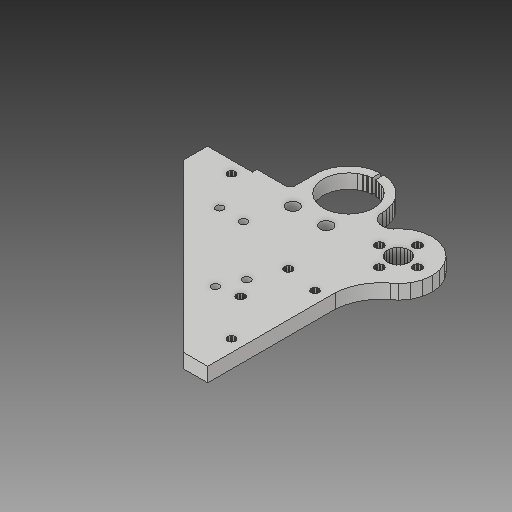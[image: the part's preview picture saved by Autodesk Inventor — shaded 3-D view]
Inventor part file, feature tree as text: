
AUTODESK INVENTOR PART (.ipt)
format: ipt  version: 2017 (Build 210142000, 142)  size: 598,016 bytes
history: native  units: mm
features: other x3, sketch x2
ambient origin geometry x8: Origin, YZ Plane, XZ Plane, XY Plane, X Axis, Y Axis, Z Axis, Center Point
bodies: Solid1 (feature_tree)
feature tree (5):
  other  "Left Bed Holder Lower.ipt"
  other  "Solid1::Left Bed Holder Lower.ipt"
  other  "TaggingFeature1"
  sketch  "Sketch2"  dims[d0=10.0mm]
  sketch  "Sketch4"
